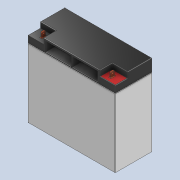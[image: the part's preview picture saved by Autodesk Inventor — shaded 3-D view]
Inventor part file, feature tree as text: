
AUTODESK INVENTOR PART (.ipt)
format: ipt  version: 2021 (Build 250183000, 183)  size: 209,920 bytes
history: native  units: in
note: dims shown in document units (in); Inventor stores cm internally (conversion verified against a paired STEP export)
features: fillet x1
ambient origin geometry x8: Origin, YZ Plane, XZ Plane, XY Plane, X Axis, Y Axis, Z Axis, Center Point
bodies: Solid1 (feature_tree)
feature tree (1):
  fillet  "Fillet4"  [1 undecoded]
note: 1 required parameter value undecoded (feature->parameter linkage not recoverable at this tier; creation-order binding heuristic only, values carry confidence <= 0.55)
